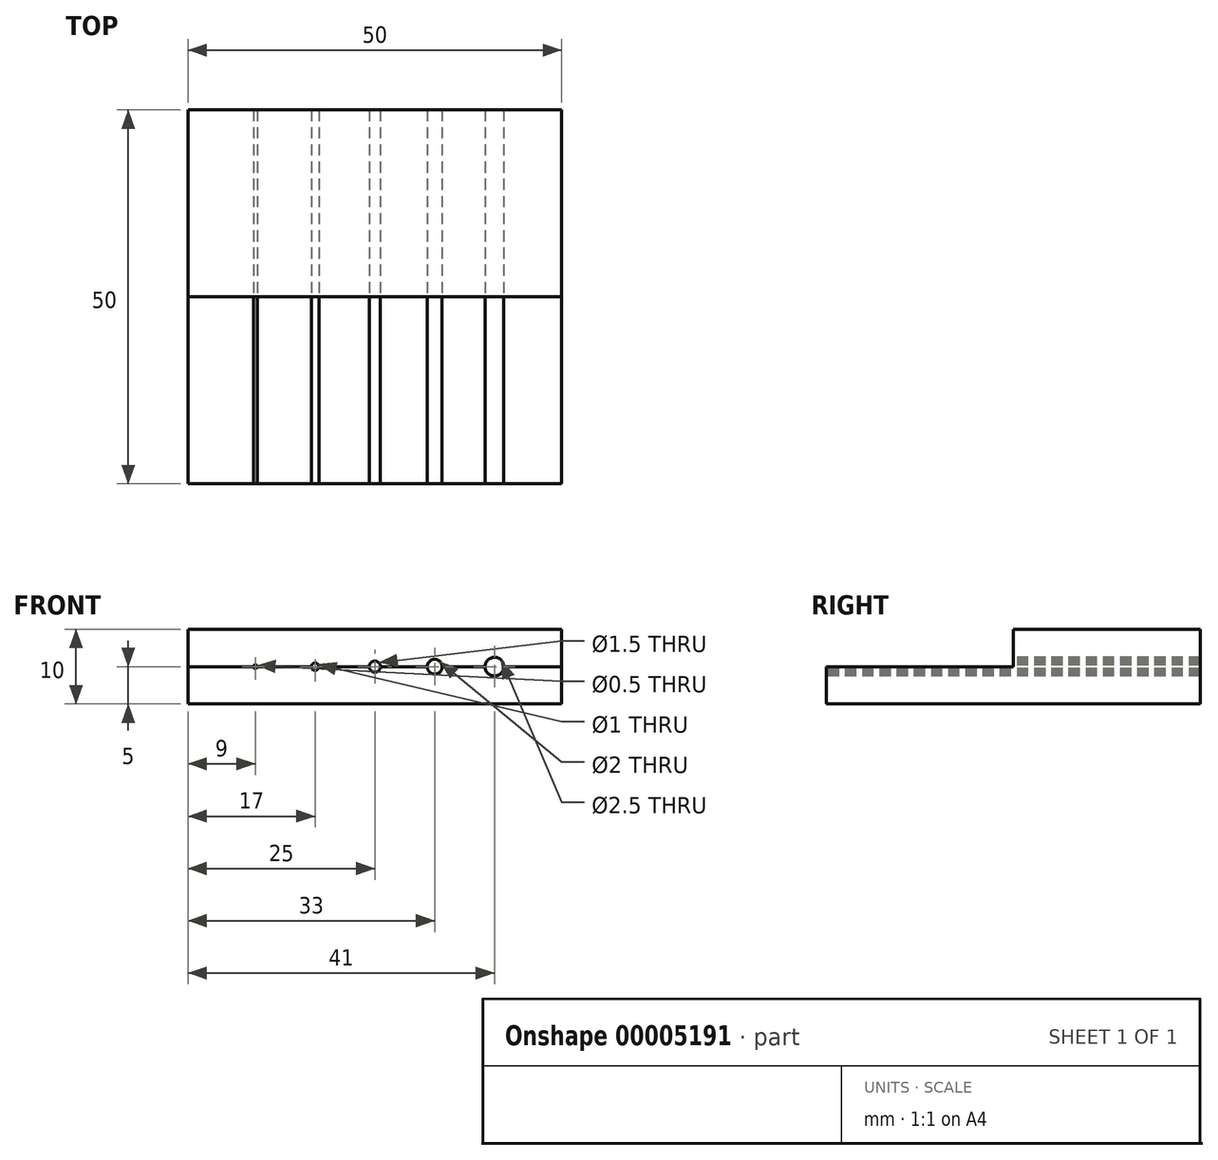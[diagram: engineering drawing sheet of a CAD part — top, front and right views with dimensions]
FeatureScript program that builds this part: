
annotation { "Feature Type Name" : "Feature", "Feature Type Description" : "" }
export const myFeature = defineFeature(function(context is Context, id is Id, definition is map)
    precondition{}
    {
        {
            var Q0;
            Q0=qCreatedBy(makeId("Top.planeOp"),FACE);
            var sketch = newSketch(context, id + "F0", { "sketchPlane" : qUnion([Q0])});
            skLineSegment(sketch, "E0.rect.bottom", {"start": v(25, 25) * mm, "end": v(-25, 25) * mm});
            skLineSegment(sketch, "E0.rect.top", {"start": v(25, -25) * mm, "end": v(-25, -25) * mm});
            skLineSegment(sketch, "E0.rect.left", {"start": v(25, 25) * mm, "end": v(25, -25) * mm});
            skLineSegment(sketch, "E0.rect.right", {"start": v(-25, 25) * mm, "end": v(-25, -25) * mm});
            skPoint(sketch, "E0.rect.middle", {"position": v(0, 0) * mm});
            skSolve(sketch);
        }
        {
            var Q0;
            Q0 = qSketchRegion(id + "F0", true);
            extrude(context, id + "F1", {"entities" : qUnion([Q0]), "depth" : 10 * mm});
        }
        {
            var Q0;
            Q0=makeQuery(id+"F1.opExtrude","SWEPT_FACE",FACE,{"disambiguationData":[OSD([sQuery(id+"F0.wireOp",EDGE,"E0.rect.top")])]});
            var sketch = newSketch(context, id + "F2", { "sketchPlane" : qUnion([Q0])});
            skLineSegment(sketch, "E1", {"start": v(-25, 5) * mm, "end": v(25, 5) * mm, "construction": true});
            skCircle(sketch, "E2", {"center": v(0, 5) * mm, "radius": 0.75 * mm});
            skCircle(sketch, "E3", {"center": v(-16, 5) * mm, "radius": 0.25 * mm});
            skCircle(sketch, "E4", {"center": v(-8, 5) * mm, "radius": 0.5 * mm});
            skCircle(sketch, "E5", {"center": v(8, 5) * mm, "radius": 1 * mm});
            skCircle(sketch, "E6", {"center": v(16, 5) * mm, "radius": 1.25 * mm});
            skSolve(sketch);
        }
        {
            var Q0;
            Q0 = qSketchRegion(id + "F2", true);
            extrude(context, id + "F3", {"entities" : qUnion([Q0]), "operationType" : NewBodyOperationType.REMOVE, "endBound" : BoundingType.THROUGH_ALL, "oppositeDirection" : true, "depth" : 25 * mm});
        }
        {
            var Q0;
            Q0=makeQuery(id+"F1.opExtrude","SWEPT_FACE",FACE,{"disambiguationData":[OSD([sQuery(id+"F0.wireOp",EDGE,"E0.rect.top")])]});
            var sketch = newSketch(context, id + "F4", { "sketchPlane" : qUnion([Q0])});
            skLineSegment(sketch, "E7.bottom", {"start": v(-25, 10) * mm, "end": v(25, 10) * mm});
            skLineSegment(sketch, "E7.top", {"start": v(-25, 5) * mm, "end": v(25, 5) * mm});
            skLineSegment(sketch, "E7.left", {"start": v(-25, 10) * mm, "end": v(-25, 5) * mm});
            skLineSegment(sketch, "E7.right", {"start": v(25, 10) * mm, "end": v(25, 5) * mm});
            skSolve(sketch);
        }
        {
            var Q0;
            Q0 = qSketchRegion(id + "F4", true);
            extrude(context, id + "F5", {"entities" : qUnion([Q0]), "operationType" : NewBodyOperationType.REMOVE, "oppositeDirection" : true, "depth" : 25 * mm});
        }
    });
